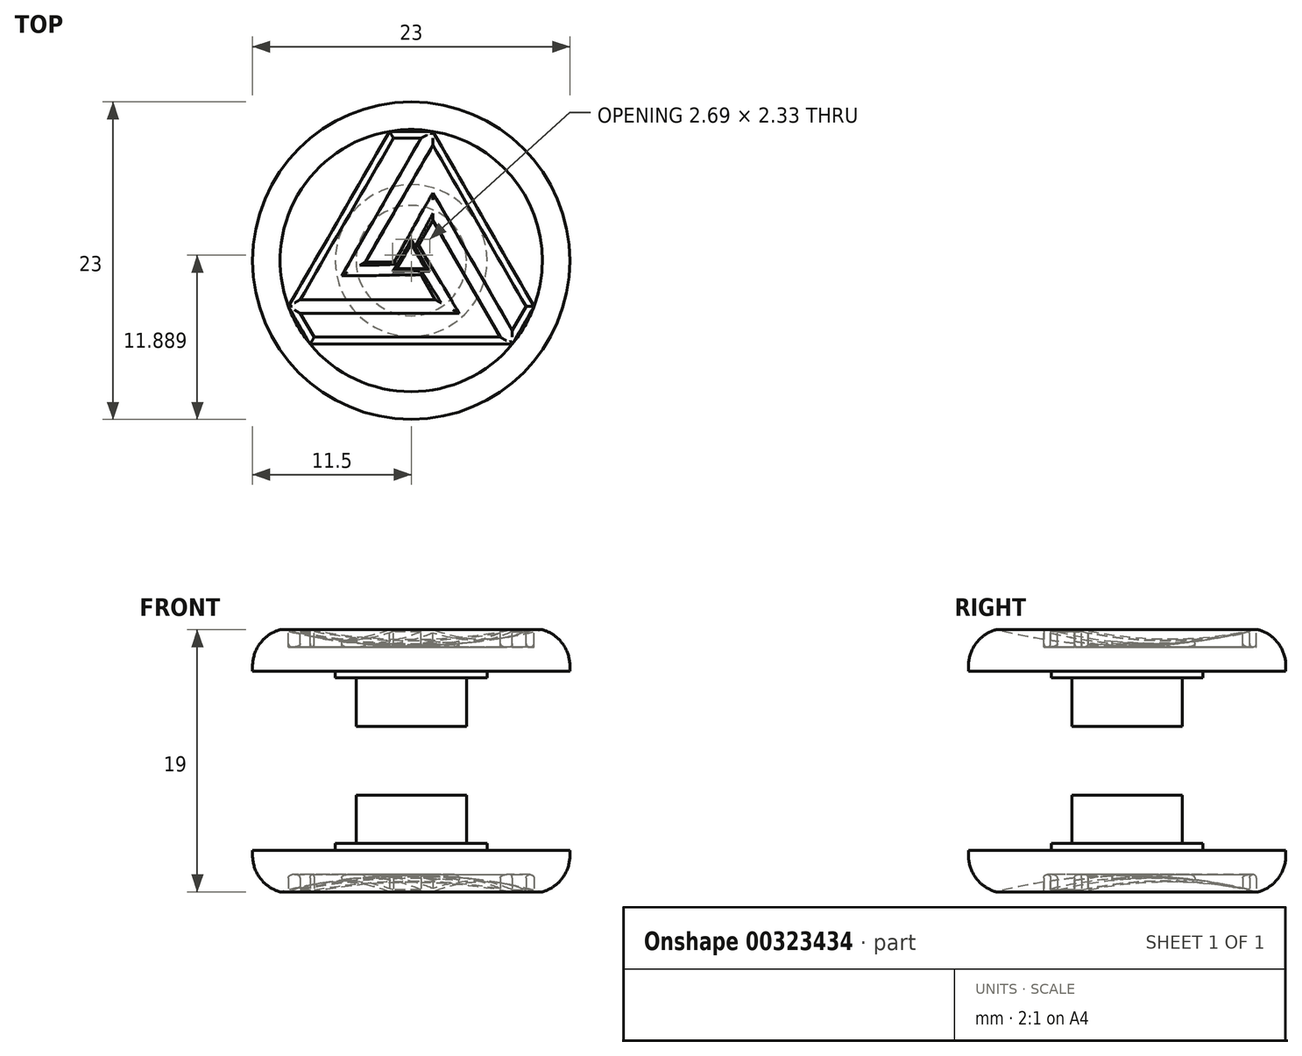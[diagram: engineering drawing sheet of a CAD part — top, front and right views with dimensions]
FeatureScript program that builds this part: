
annotation { "Feature Type Name" : "Feature", "Feature Type Description" : "" }
export const myFeature = defineFeature(function(context is Context, id is Id, definition is map)
    precondition{}
    {
        {
            var Q0;
            Q0=qCreatedBy(makeId("Right.planeOp"),FACE);
            var sketch = newSketch(context, id + "F0", { "sketchPlane" : qUnion([Q0])});
            skLineSegment(sketch, "E0", {"start": v(0, 0) * mm, "end": v(-4, 0) * mm});
            skLineSegment(sketch, "E1", {"start": v(-4, 0) * mm, "end": v(-4, 3.5) * mm});
            skLineSegment(sketch, "E2", {"start": v(-4, 3.5) * mm, "end": v(-5.5, 3.5) * mm});
            skLineSegment(sketch, "E3", {"start": v(-5.5, 3.5) * mm, "end": v(-5.5, 4) * mm});
            skLineSegment(sketch, "E4", {"start": v(-5.5, 4) * mm, "end": v(-11.5, 4) * mm});
            skLineSegment(sketch, "E5", {"start": v(-11.5, 4) * mm, "end": v(-11.5, 5.5) * mm});
            skLineSegment(sketch, "E6", {"start": v(-11.5, 5.5) * mm, "end": v(-10, 7) * mm});
            skLineSegment(sketch, "E7", {"start": v(0, 5.8) * mm, "end": v(0, 0) * mm});
            skArc(sketch, "E8", {"start": v(-9.5, 7) * mm, "mid": v(-4.79, 6.11) * mm, "end": v(0, 5.8) * mm});
            skPoint(sketch, "E9.orphan", {"position": v(10, 7) * mm});
            skLineSegment(sketch, "E10", {"start": v(-10, 7) * mm, "end": v(-9.5, 7) * mm});
            skLineSegment(sketch, "E11", {"start": v(-9.5, 7) * mm, "end": v(0, 7) * mm, "construction": true});
            skLineSegment(sketch, "E12", {"start": v(0, 7) * mm, "end": v(0, 5.8) * mm, "construction": true});
            skSolve(sketch);
        }
        {
            var Q0;
            Q0=makeQuery(id+"F0.imprint","IMPRINT",FACE,{"disambiguationData":[TD([[makeQuery(id+"F0.imprint","IMPRINT",EDGE,{"derivedFrom":sQuery(id+"F0.wireOp",EDGE,"E0")}),-1.0]])]});
            var Q1;
            Q1=sQuery(id+"F0.wireOp",EDGE,"E7");
            revolve(context, id + "F1", {"entities" : qUnion([Q0]), "axis" : qUnion([Q1]), "revolveType" : RevolveType.FULL});
        }
        {
            var Q0;
            Q0=makeQuery(id+"F1.opRevolve","SWEPT_FACE",FACE,{"disambiguationData":[OSD([sQuery(id+"F0.wireOp",EDGE,"E10")])]});
            var sketch = newSketch(context, id + "F2", { "sketchPlane" : qUnion([Q0])});
            skCircle(sketch, "E13.cCircle", {"center": v(0, 0) * mm, "radius": 12.1 * mm, "construction": true});
            skLineSegment(sketch, "E13.0", {"start": v(1.57, 9.37) * mm, "end": v(8.9, -3.32) * mm});
            skLineSegment(sketch, "E13.1", {"start": v(7.33, -6.05) * mm, "end": v(-7.33, -6.05) * mm});
            skLineSegment(sketch, "E13.2", {"start": v(-8.9, -3.32) * mm, "end": v(-1.57, 9.37) * mm});
            skCircle(sketch, "E14.cCircle", {"center": v(0, 0) * mm, "radius": 6.64 * mm, "construction": true});
            skLineSegment(sketch, "E14.0", {"start": v(1.57, 3.91) * mm, "end": v(7.33, -6.05) * mm});
            skLineSegment(sketch, "E14.1", {"start": v(2.6, -3.32) * mm, "end": v(-8.9, -3.32) * mm});
            skLineSegment(sketch, "E14.2", {"start": v(-4.18, -0.6) * mm, "end": v(1.57, 9.37) * mm});
            skCircle(sketch, "E15.cCircle", {"center": v(0, 0) * mm, "radius": 1.19 * mm, "construction": true});
            skLineSegment(sketch, "E15.0", {"start": v(0, 1.19) * mm, "end": v(1.03, -0.6) * mm});
            skLineSegment(sketch, "E15.1", {"start": v(1.03, -0.6) * mm, "end": v(-1.03, -0.6) * mm});
            skLineSegment(sketch, "E15.2", {"start": v(-1.03, -0.6) * mm, "end": v(0, 1.19) * mm});
            skLineSegment(sketch, "E16", {"start": v(-0.79, -0.18) * mm, "end": v(-3.15, 1.19) * mm, "construction": true});
            skLineSegment(sketch, "E17", {"start": v(-3.15, 1.19) * mm, "end": v(-5.51, 2.55) * mm, "construction": true});
            skLineSegment(sketch, "E18", {"start": v(0, 6.64) * mm, "end": v(1.57, 9.37) * mm, "construction": true});
            skLineSegment(sketch, "E19", {"start": v(0, 6.64) * mm, "end": v(-1.57, 9.37) * mm, "construction": true});
            skLineSegment(sketch, "E20", {"start": v(-1.57, 9.37) * mm, "end": v(1.57, 9.37) * mm});
            skLineSegment(sketch, "E21", {"start": v(8.9, -3.32) * mm, "end": v(7.33, -6.05) * mm});
            skLineSegment(sketch, "E22", {"start": v(-7.33, -6.05) * mm, "end": v(-8.9, -3.32) * mm});
            skLineSegment(sketch, "E23", {"start": v(1.03, -0.6) * mm, "end": v(2.6, -3.32) * mm});
            skLineSegment(sketch, "E24", {"start": v(-1.03, -0.6) * mm, "end": v(-4.18, -0.6) * mm});
            skLineSegment(sketch, "E25", {"start": v(0, 1.19) * mm, "end": v(1.57, 3.91) * mm});
            skPoint(sketch, "E26.orphan", {"position": v(5.75, -3.32) * mm});
            skPoint(sketch, "E27.orphan", {"position": v(-5.75, -3.32) * mm});
            skPoint(sketch, "E28.orphan", {"position": v(0, 12.1) * mm});
            skPoint(sketch, "E29.orphan", {"position": v(10.48, -6.05) * mm});
            skPoint(sketch, "E30.orphan", {"position": v(-10.48, -6.05) * mm});
            skLineSegment(sketch, "E31.0", {"start": v(1.74, -2.82) * mm, "end": v(-8.03, -2.82) * mm});
            skLineSegment(sketch, "E31.1", {"start": v(0.74, -1.1) * mm, "end": v(1.74, -2.82) * mm});
            skLineSegment(sketch, "E31.2", {"start": v(-1.29, 8.87) * mm, "end": v(0.7, 8.87) * mm});
            skLineSegment(sketch, "E31.3", {"start": v(-5.04, -1.1) * mm, "end": v(0.7, 8.87) * mm});
            skLineSegment(sketch, "E31.4", {"start": v(-1.2, -1.1) * mm, "end": v(-5.04, -1.1) * mm});
            skLineSegment(sketch, "E31.5", {"start": v(-8.03, -2.82) * mm, "end": v(-1.29, 8.87) * mm});
            skLineSegment(sketch, "E31.6", {"start": v(0.74, -1.1) * mm, "end": v(-1.2, -1.1) * mm});
            skLineSegment(sketch, "E32.0", {"start": v(-3.31, -0.1) * mm, "end": v(1.57, 8.37) * mm});
            skLineSegment(sketch, "E32.1", {"start": v(-1.32, -0.1) * mm, "end": v(-3.31, -0.1) * mm});
            skLineSegment(sketch, "E32.2", {"start": v(8.32, -3.32) * mm, "end": v(7.33, -5.05) * mm});
            skLineSegment(sketch, "E32.3", {"start": v(1.57, 4.91) * mm, "end": v(7.33, -5.05) * mm});
            skLineSegment(sketch, "E32.4", {"start": v(-0.57, 1.2) * mm, "end": v(1.57, 4.91) * mm});
            skLineSegment(sketch, "E32.5", {"start": v(1.57, 8.37) * mm, "end": v(8.32, -3.32) * mm});
            skLineSegment(sketch, "E32.6", {"start": v(-1.32, -0.1) * mm, "end": v(-0.57, 1.2) * mm});
            skLineSegment(sketch, "E33.0", {"start": v(1.77, -0.87) * mm, "end": v(3.47, -3.82) * mm});
            skLineSegment(sketch, "E33.1", {"start": v(0.58, 1.19) * mm, "end": v(1.77, -0.87) * mm});
            skLineSegment(sketch, "E33.2", {"start": v(-7.04, -5.55) * mm, "end": v(-8.03, -3.82) * mm});
            skLineSegment(sketch, "E33.3", {"start": v(6.46, -5.55) * mm, "end": v(-7.04, -5.55) * mm});
            skLineSegment(sketch, "E33.4", {"start": v(1.57, 2.91) * mm, "end": v(6.46, -5.55) * mm});
            skLineSegment(sketch, "E33.5", {"start": v(3.47, -3.82) * mm, "end": v(-8.03, -3.82) * mm});
            skLineSegment(sketch, "E33.6", {"start": v(0.58, 1.19) * mm, "end": v(1.57, 2.91) * mm});
            skSolve(sketch);
        }
        {
            var Q0;
            Q0=makeQuery(id+"F2.imprint","IMPRINT",FACE,{"disambiguationData":[TD([[makeQuery(id+"F2.imprint","IMPRINT",EDGE,{"derivedFrom":sQuery(id+"F2.wireOp",EDGE,"E13.1")}),-1.0]])]});
            var Q1;
            Q1=makeQuery(id+"F2.imprint","IMPRINT",FACE,{"disambiguationData":[TD([[makeQuery(id+"F2.imprint","IMPRINT",EDGE,{"derivedFrom":sQuery(id+"F2.wireOp",EDGE,"E13.2")}),-1.0]])]});
            var Q2;
            Q2=makeQuery(id+"F2.imprint","IMPRINT",FACE,{"disambiguationData":[TD([[makeQuery(id+"F2.imprint","IMPRINT",EDGE,{"derivedFrom":sQuery(id+"F2.wireOp",EDGE,"E13.0")}),-1.0]])]});
            extrude(context, id + "F3", {"entities" : qUnion([Q0, Q1, Q2]), "operationType" : NewBodyOperationType.REMOVE, "oppositeDirection" : true, "depth" : 1.25 * mm, "offsetDistance" : 25 * mm});
        }
        {
            var Q0;
            Q0=makeQuery(id+"F1.opRevolve","SWEPT_EDGE",EDGE,{"disambiguationData":[OSD([sQuery(id+"F0.wireOp",EDGE,"E6"),sQuery(id+"F0.wireOp",EDGE,"E10")])]});
            var Q1;
            Q1=makeQuery(id+"F1.opRevolve","SWEPT_EDGE",EDGE,{"disambiguationData":[OSD([sQuery(id+"F0.wireOp",EDGE,"E5"),sQuery(id+"F0.wireOp",EDGE,"E6")])]});
            fillet(context, id + "F4", {"entities" : qUnion([Q0, Q1]), "radius" : 2.73 * mm, "tangentPropagation" : true, "allowEdgeOverflow" : false});
        }
        {
            var Q0;
            Q0=makeQuery(id+"F3.boolean.opBoolean","COPY",FACE,{"derivedFrom":makeQuery(id+"F3.opExtrude","CAP_FACE",FACE,{"disambiguationData":[OSD([sQuery(id+"F2.wireOp",EDGE,"E13.0"),sQuery(id+"F2.wireOp",EDGE,"E13.1"),sQuery(id+"F2.wireOp",EDGE,"E13.2"),sQuery(id+"F2.wireOp",EDGE,"E15.0"),sQuery(id+"F2.wireOp",EDGE,"E15.1"),sQuery(id+"F2.wireOp",EDGE,"E15.2"),sQuery(id+"F2.wireOp",EDGE,"E20"),sQuery(id+"F2.wireOp",EDGE,"E21"),sQuery(id+"F2.wireOp",EDGE,"E22"),sQuery(id+"F2.wireOp",EDGE,"E31.0"),sQuery(id+"F2.wireOp",EDGE,"E31.1"),sQuery(id+"F2.wireOp",EDGE,"E31.2"),sQuery(id+"F2.wireOp",EDGE,"E31.3"),sQuery(id+"F2.wireOp",EDGE,"E31.4"),sQuery(id+"F2.wireOp",EDGE,"E31.5"),sQuery(id+"F2.wireOp",EDGE,"E31.6"),sQuery(id+"F2.wireOp",EDGE,"E32.0"),sQuery(id+"F2.wireOp",EDGE,"E32.1"),sQuery(id+"F2.wireOp",EDGE,"E32.2"),sQuery(id+"F2.wireOp",EDGE,"E32.3"),sQuery(id+"F2.wireOp",EDGE,"E32.4"),sQuery(id+"F2.wireOp",EDGE,"E32.5"),sQuery(id+"F2.wireOp",EDGE,"E32.6"),sQuery(id+"F2.wireOp",EDGE,"E33.0"),sQuery(id+"F2.wireOp",EDGE,"E33.1"),sQuery(id+"F2.wireOp",EDGE,"E33.2"),sQuery(id+"F2.wireOp",EDGE,"E33.3"),sQuery(id+"F2.wireOp",EDGE,"E33.4"),sQuery(id+"F2.wireOp",EDGE,"E33.5"),sQuery(id+"F2.wireOp",EDGE,"E33.6")])],"isStart":false})});
            fillet(context, id + "F5", {"entities" : qUnion([Q0]), "radius" : .25 * mm, "tangentPropagation" : true, "allowEdgeOverflow" : false});
        }
        {
            var Q0;
            Q0=makeQuery(id+"F1.opRevolve","SWEPT_FACE",FACE,{"disambiguationData":[OSD([sQuery(id+"F0.wireOp",EDGE,"E0")])]});
            cPlane(context, id + "F6", {"entities" : qUnion([Q0]), "cplaneType" : CPlaneType.OFFSET, "offset" : 2.5 * mm, "width" : 150 * mm, "height" : 150 * mm});
        }
        {
            var Q0;
            Q0=makeQuery(id+"F1.opRevolve","SWEPT_BODY",BODY,{"disambiguationData":[OSD([sQuery(id+"F0.wireOp",EDGE,"E0"),sQuery(id+"F0.wireOp",EDGE,"E1"),sQuery(id+"F0.wireOp",EDGE,"E2"),sQuery(id+"F0.wireOp",EDGE,"E3"),sQuery(id+"F0.wireOp",EDGE,"E4"),sQuery(id+"F0.wireOp",EDGE,"E5"),sQuery(id+"F0.wireOp",EDGE,"E6"),sQuery(id+"F0.wireOp",EDGE,"E7"),sQuery(id+"F0.wireOp",EDGE,"E8"),sQuery(id+"F0.wireOp",EDGE,"E10")])]});
            var Q1;
            Q1=qCreatedBy(id+"F6.planeOp",FACE);
            mirror(context, id + "F7", {"entities" : qUnion([Q0]), "mirrorPlane" : qUnion([Q1])});
        }
    });
